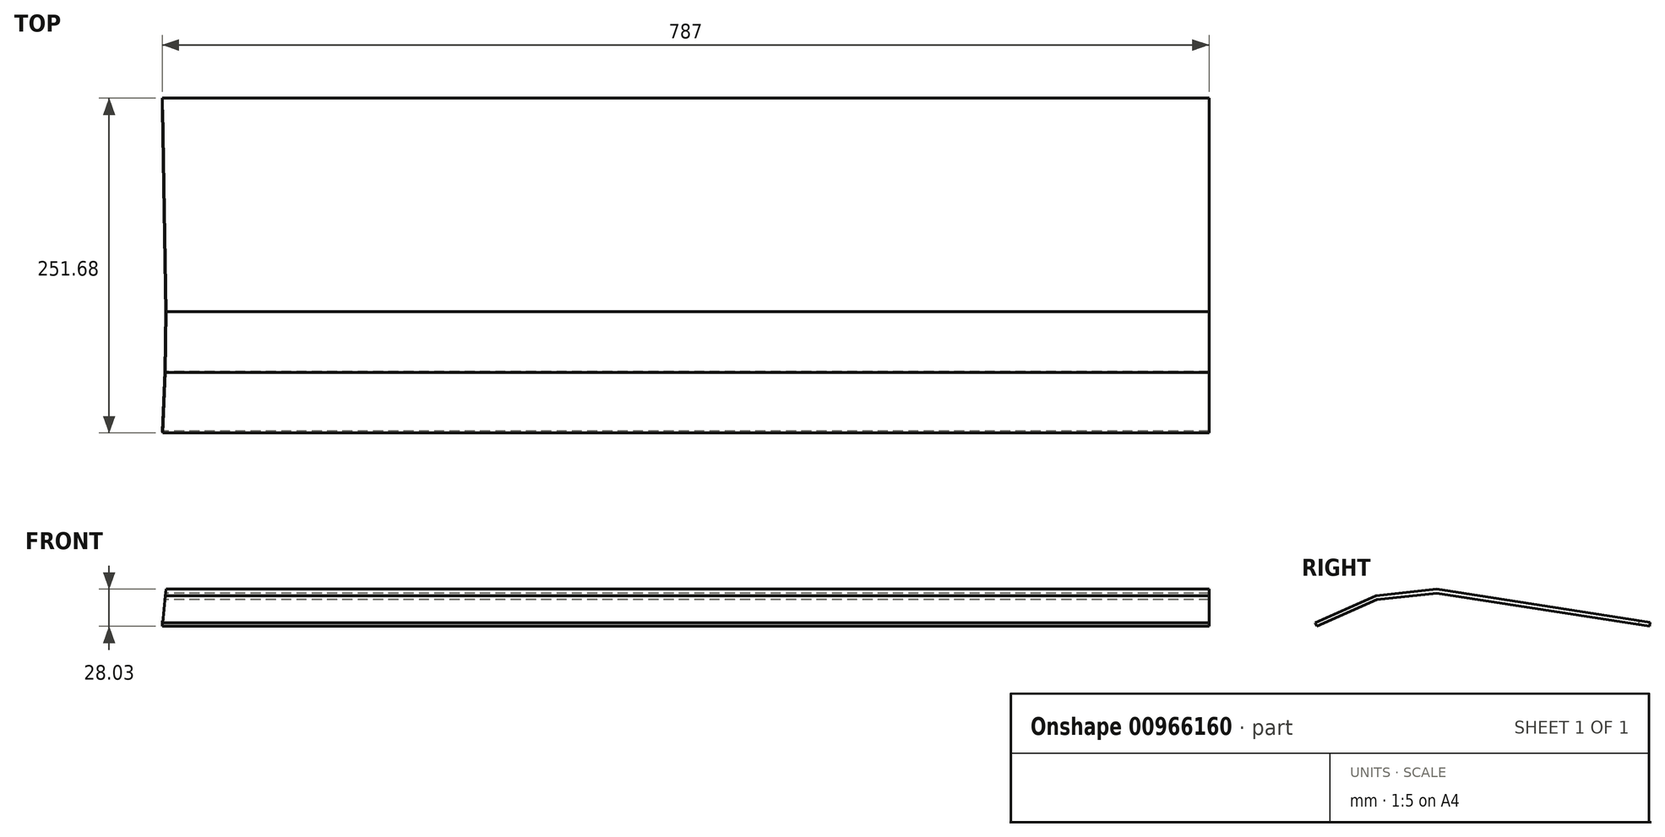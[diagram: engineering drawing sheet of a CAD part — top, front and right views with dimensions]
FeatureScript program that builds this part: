
annotation { "Feature Type Name" : "Feature", "Feature Type Description" : "" }
export const myFeature = defineFeature(function(context is Context, id is Id, definition is map)
    precondition{}
    {
        {
            var Q0;
            Q0=qCreatedBy(makeId("Right.planeOp"),FACE);
            var sketch = newSketch(context, id + "F0", { "sketchPlane" : qUnion([Q0])});
            skLineSegment(sketch, "E0", {"start": v(-91.75, 0) * mm, "end": v(-46.75, 20) * mm});
            skLineSegment(sketch, "E1", {"start": v(-46.75, 20) * mm, "end": v(-1.75, 25) * mm});
            skLineSegment(sketch, "E2", {"start": v(-1.75, 25) * mm, "end": v(158.25, 0) * mm});
            skLineSegment(sketch, "E3.0", {"start": v(-1.69, 28.03) * mm, "end": v(158.71, 2.96) * mm});
            skLineSegment(sketch, "E3.1", {"start": v(-47.55, 22.93) * mm, "end": v(-1.69, 28.03) * mm});
            skLineSegment(sketch, "E3.2", {"start": v(-92.97, 2.74) * mm, "end": v(-47.55, 22.93) * mm});
            skLineSegment(sketch, "E4", {"start": v(-91.75, 0) * mm, "end": v(-92.97, 2.74) * mm});
            skLineSegment(sketch, "E5", {"start": v(158.25, 0) * mm, "end": v(158.71, 2.96) * mm});
            skSolve(sketch);
        }
        {
            var Q0;
            Q0=makeQuery(id+"F0.imprint","IMPRINT",FACE,{"disambiguationData":[TD([[makeQuery(id+"F0.imprint","IMPRINT",EDGE,{"derivedFrom":sQuery(id+"F0.wireOp",EDGE,"E1")}),1.0]])]});
            var Q1;
            Q1=makeQuery(id+"F0.imprint","IMPRINT",FACE,{"disambiguationData":[TD([[makeQuery(id+"F0.imprint","IMPRINT",EDGE,{"derivedFrom":sQuery(id+"F0.wireOp",EDGE,"E0")}),1.0]])]});
            var Q2;
            Q2=makeQuery(id+"F0.imprint","IMPRINT",FACE,{"disambiguationData":[TD([[makeQuery(id+"F0.imprint","IMPRINT",EDGE,{"derivedFrom":sQuery(id+"F0.wireOp",EDGE,"E2")}),1.0]])]});
            extrude(context, id + "F1", {"entities" : qUnion([Q0, Q1, Q2]), "depth" : 787 * mm, "offsetDistance" : 25 * mm});
        }
        {
            var Q0;
            Q0=qCreatedBy(makeId("Front.planeOp"),FACE);
            var sketch = newSketch(context, id + "F2", { "sketchPlane" : qUnion([Q0])});
            skPoint(sketch, "E6.middle", {"position": v(0, 0) * mm});
            skLineSegment(sketch, "E7", {"start": v(0, 0) * mm, "end": v(32.96, -3.46) * mm, "construction": true});
            skLineSegment(sketch, "E8.bottom", {"start": v(0, 0) * mm, "end": v(-49.73, 5.23) * mm});
            skLineSegment(sketch, "E8.top", {"start": v(5.23, 49.73) * mm, "end": v(-44.5, 54.95) * mm});
            skLineSegment(sketch, "E8.left", {"start": v(0, 0) * mm, "end": v(5.23, 49.73) * mm});
            skLineSegment(sketch, "E8.right", {"start": v(-49.73, 5.23) * mm, "end": v(-44.5, 54.95) * mm});
            skSolve(sketch);
        }
        {
            var Q0;
            Q0=makeQuery(id+"F2.imprint","IMPRINT",FACE,{"disambiguationData":[TD([[makeQuery(id+"F2.imprint","IMPRINT",EDGE,{"derivedFrom":sQuery(id+"F2.wireOp",EDGE,"E8.bottom")}),-1.0]])]});
            extrude(context, id + "F3", {"entities" : qUnion([Q0]), "operationType" : NewBodyOperationType.REMOVE, "endBound" : BoundingType.SYMMETRIC, "depth" : 300 * mm, "offsetDistance" : 25 * mm});
        }
    });
